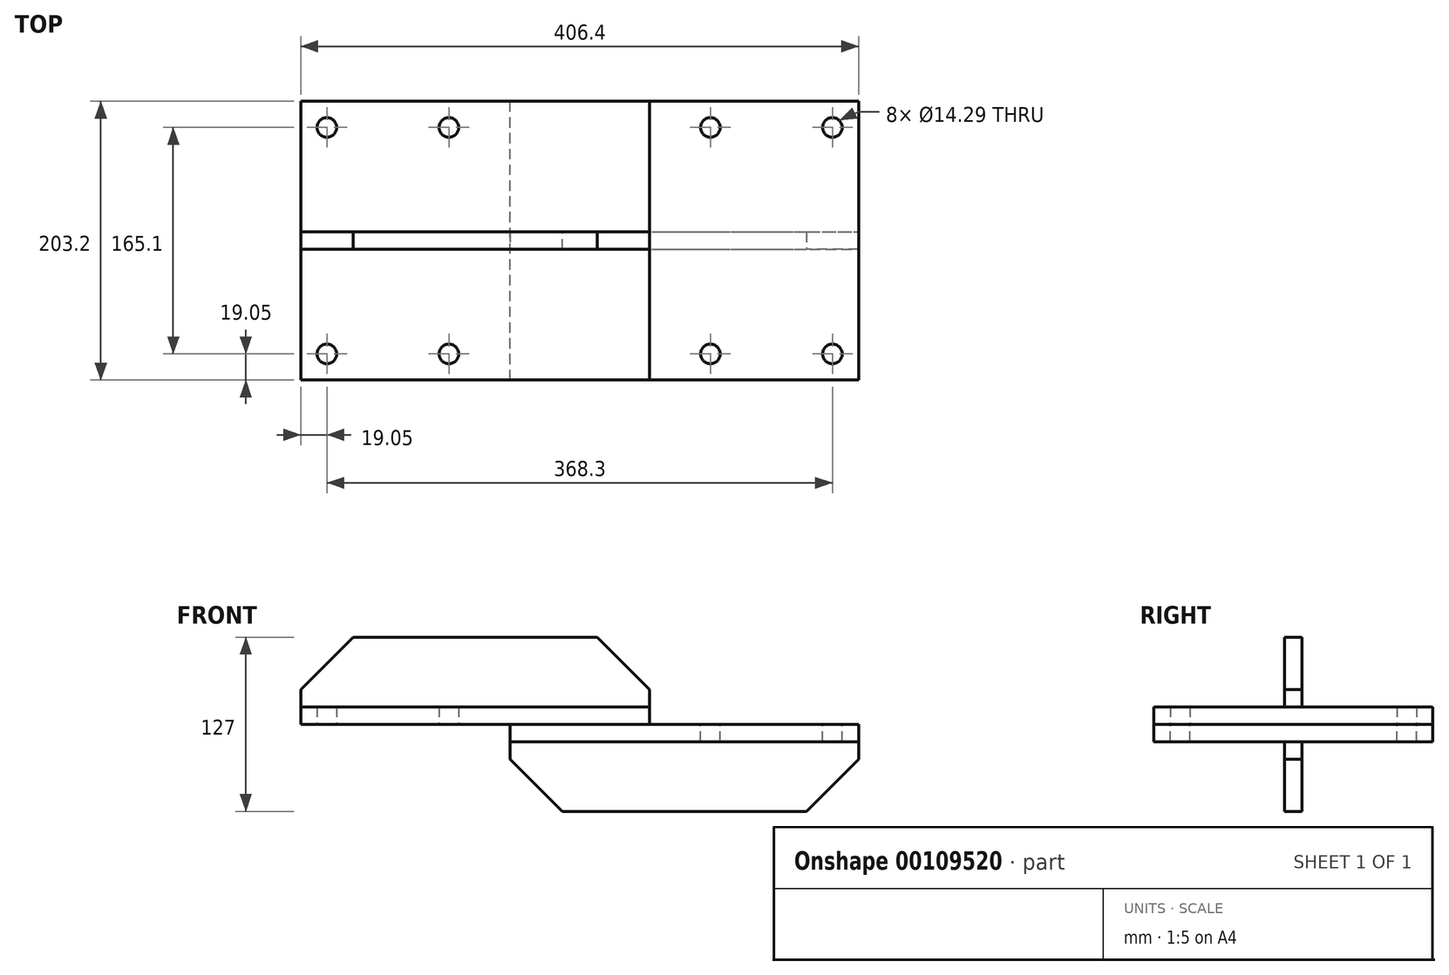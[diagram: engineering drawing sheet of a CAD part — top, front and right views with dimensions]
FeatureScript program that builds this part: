
annotation { "Feature Type Name" : "Feature", "Feature Type Description" : "" }
export const myFeature = defineFeature(function(context is Context, id is Id, definition is map)
    precondition{}
    {
        {
            var Q0;
            Q0=qCreatedBy(makeId("Top.planeOp"),FACE);
            var sketch = newSketch(context, id + "F0", { "sketchPlane" : qUnion([Q0])});
            skLineSegment(sketch, "E0", {"start": v(0, 106.75) * mm, "end": v(0, -105.6) * mm, "construction": true});
            skLineSegment(sketch, "E1.0", {"start": v(-203.2, 106.75) * mm, "end": v(-203.2, -105.6) * mm, "construction": true});
            skLineSegment(sketch, "E2.MirrorCS", {"start": v(203.2, 106.75) * mm, "end": v(203.2, -105.6) * mm, "construction": true});
            skLineSegment(sketch, "E3", {"start": v(-283.64, 0) * mm, "end": v(308.6, 0) * mm, "construction": true});
            skLineSegment(sketch, "E4.0", {"start": v(-283.64, -101.6) * mm, "end": v(308.6, -101.6) * mm, "construction": true});
            skLineSegment(sketch, "E5.bottom", {"start": v(-203.2, -101.6) * mm, "end": v(50.8, -101.6) * mm});
            skLineSegment(sketch, "E5.top", {"start": v(-203.2, 101.6) * mm, "end": v(50.8, 101.6) * mm});
            skLineSegment(sketch, "E5.left", {"start": v(-203.2, -101.6) * mm, "end": v(-203.2, 101.6) * mm});
            skLineSegment(sketch, "E5.right", {"start": v(50.8, -101.6) * mm, "end": v(50.8, 101.6) * mm});
            skLineSegment(sketch, "E6.0", {"start": v(-139.7, -101.6) * mm, "end": v(-139.7, 101.6) * mm, "construction": true});
            skLineSegment(sketch, "E7.0", {"start": v(-184.15, -101.6) * mm, "end": v(-184.15, 101.6) * mm, "construction": true});
            skLineSegment(sketch, "E8.0", {"start": v(-283.64, -82.55) * mm, "end": v(308.6, -82.55) * mm, "construction": true});
            skCircle(sketch, "E9", {"center": v(-184.15, -82.55) * mm, "radius": 7.14 * mm});
            skCircle(sketch, "E10.MirrorC", {"center": v(-95.25, -82.55) * mm, "radius": 7.14 * mm});
            skCircle(sketch, "E11.MirrorC", {"center": v(-95.25, 82.55) * mm, "radius": 7.14 * mm});
            skCircle(sketch, "E12.MirrorC", {"center": v(-184.15, 82.55) * mm, "radius": 7.14 * mm});
            skSolve(sketch);
        }
        {
            var Q0;
            Q0=makeQuery(id+"F0.imprint","IMPRINT",FACE,{"disambiguationData":[TD([[makeQuery(id+"F0.imprint","IMPRINT",EDGE,{"derivedFrom":sQuery(id+"F0.wireOp",EDGE,"E5.bottom")}),1.0]])]});
            extrude(context, id + "F1", {"entities" : qUnion([Q0]), "depth" : 12.7 * mm});
        }
        {
            var Q0;
            Q0=makeQuery(id+"F1.opExtrude","CAP_FACE",FACE,{"disambiguationData":[OSD([sQuery(id+"F0.wireOp",EDGE,"E5.bottom"),sQuery(id+"F0.wireOp",EDGE,"E5.top"),sQuery(id+"F0.wireOp",EDGE,"E5.left"),sQuery(id+"F0.wireOp",EDGE,"E5.right"),sQuery(id+"F0.wireOp",EDGE,"E9"),sQuery(id+"F0.wireOp",EDGE,"E10.MirrorC"),sQuery(id+"F0.wireOp",EDGE,"E11.MirrorC"),sQuery(id+"F0.wireOp",EDGE,"E12.MirrorC")])],"isStart":true});
            var sketch = newSketch(context, id + "F2", { "sketchPlane" : qUnion([Q0])});
            skLineSegment(sketch, "E13.0", {"start": v(-283.64, 101.6) * mm, "end": v(308.6, 101.6) * mm, "construction": true});
            skLineSegment(sketch, "E14.0", {"start": v(203.2, -106.75) * mm, "end": v(203.2, 105.6) * mm, "construction": true});
            skLineSegment(sketch, "E15.bottom", {"start": v(203.2, 101.6) * mm, "end": v(-50.8, 101.6) * mm});
            skLineSegment(sketch, "E15.top", {"start": v(203.2, -101.6) * mm, "end": v(-50.8, -101.6) * mm});
            skLineSegment(sketch, "E15.left", {"start": v(203.2, 101.6) * mm, "end": v(203.2, -101.6) * mm});
            skLineSegment(sketch, "E15.right", {"start": v(-50.8, 101.6) * mm, "end": v(-50.8, -101.6) * mm});
            skLineSegment(sketch, "E16.0", {"start": v(139.7, 101.6) * mm, "end": v(139.7, -101.6) * mm, "construction": true});
            skLineSegment(sketch, "E17.0", {"start": v(184.15, 101.6) * mm, "end": v(184.15, -101.6) * mm, "construction": true});
            skLineSegment(sketch, "E18.0", {"start": v(-283.64, 82.55) * mm, "end": v(308.6, 82.55) * mm, "construction": true});
            skCircle(sketch, "E19", {"center": v(184.15, 82.55) * mm, "radius": 7.14 * mm});
            skCircle(sketch, "E20.MirrorC", {"center": v(95.25, 82.55) * mm, "radius": 7.14 * mm});
            skCircle(sketch, "E21.MirrorC", {"center": v(95.25, -82.55) * mm, "radius": 7.14 * mm});
            skCircle(sketch, "E22.MirrorC", {"center": v(184.15, -82.55) * mm, "radius": 7.14 * mm});
            skSolve(sketch);
        }
        {
            var Q0;
            Q0=qSketchRegion(id+"F2",true);
            extrude(context, id + "F3", {"entities" : qUnion([Q0]), "depth" : 12.7 * mm});
        }
        {
            var Q0;
            Q0=makeQuery(id+"F1.opExtrude","CAP_FACE",FACE,{"disambiguationData":[OSD([sQuery(id+"F0.wireOp",EDGE,"E5.bottom"),sQuery(id+"F0.wireOp",EDGE,"E5.top"),sQuery(id+"F0.wireOp",EDGE,"E5.left"),sQuery(id+"F0.wireOp",EDGE,"E5.right"),sQuery(id+"F0.wireOp",EDGE,"E9"),sQuery(id+"F0.wireOp",EDGE,"E10.MirrorC"),sQuery(id+"F0.wireOp",EDGE,"E11.MirrorC"),sQuery(id+"F0.wireOp",EDGE,"E12.MirrorC")])],"isStart":false});
            var sketch = newSketch(context, id + "F4", { "sketchPlane" : qUnion([Q0])});
            skLineSegment(sketch, "E23.0", {"start": v(-283.64, 0) * mm, "end": v(308.6, 0) * mm, "construction": true});
            skLineSegment(sketch, "E24.0", {"start": v(-203.2, -6.35) * mm, "end": v(50.8, -6.35) * mm});
            skLineSegment(sketch, "E25.0", {"start": v(-203.2, -6.35) * mm, "end": v(-203.2, 6.35) * mm});
            skLineSegment(sketch, "E26.0", {"start": v(50.8, -6.35) * mm, "end": v(50.8, 6.35) * mm});
            skLineSegment(sketch, "E27.MirrorCS", {"start": v(-203.2, 6.35) * mm, "end": v(50.8, 6.35) * mm});
            skPoint(sketch, "E28.orphan", {"position": v(-283.64, 6.35) * mm});
            skPoint(sketch, "E29.orphan", {"position": v(-283.64, -6.35) * mm});
            skPoint(sketch, "E30.orphan", {"position": v(308.6, 6.35) * mm});
            skPoint(sketch, "E31.orphan", {"position": v(308.6, -6.35) * mm});
            skPoint(sketch, "E32.orphan", {"position": v(50.8, 101.6) * mm});
            skPoint(sketch, "E33.orphan", {"position": v(50.8, -101.6) * mm});
            skPoint(sketch, "E34.orphan", {"position": v(-203.2, -101.6) * mm});
            skPoint(sketch, "E35.orphan", {"position": v(-203.2, 101.6) * mm});
            skSolve(sketch);
        }
        {
            var Q0;
            Q0=qSketchRegion(id+"F4",true);
            extrude(context, id + "F5", {"entities" : qUnion([Q0]), "depth" : 50.8 * mm});
        }
        {
            var Q0;
            Q0=makeQuery(id+"F5.opExtrude","CAP_EDGE",EDGE,{"disambiguationData":[OSD([sQuery(id+"F4.wireOp",EDGE,"E25.0")])],"isStart":false});
            var Q1;
            Q1=makeQuery(id+"F5.opExtrude","CAP_EDGE",EDGE,{"disambiguationData":[OSD([sQuery(id+"F4.wireOp",EDGE,"E26.0")])],"isStart":false});
            chamfer(context, id + "F6", {"entities" : qUnion([Q0, Q1]), "width" : 38.1 * mm, "tangentPropagation" : true});
        }
        {
            var Q0;
            Q0=makeQuery(id+"F3.opExtrude","CAP_FACE",FACE,{"disambiguationData":[OSD([sQuery(id+"F2.wireOp",EDGE,"E15.bottom"),sQuery(id+"F2.wireOp",EDGE,"E15.top"),sQuery(id+"F2.wireOp",EDGE,"E15.left"),sQuery(id+"F2.wireOp",EDGE,"E15.right"),sQuery(id+"F2.wireOp",EDGE,"E19"),sQuery(id+"F2.wireOp",EDGE,"E20.MirrorC"),sQuery(id+"F2.wireOp",EDGE,"E21.MirrorC"),sQuery(id+"F2.wireOp",EDGE,"E22.MirrorC")])],"isStart":false});
            var sketch = newSketch(context, id + "F7", { "sketchPlane" : qUnion([Q0])});
            skLineSegment(sketch, "E36.0", {"start": v(-283.64, 0) * mm, "end": v(308.6, 0) * mm, "construction": true});
            skLineSegment(sketch, "E37.0", {"start": v(-50.8, 101.6) * mm, "end": v(-50.8, -101.6) * mm});
            skLineSegment(sketch, "E38.0", {"start": v(203.2, -106.75) * mm, "end": v(203.2, 105.6) * mm});
            skLineSegment(sketch, "E39.0", {"start": v(-283.64, -6.35) * mm, "end": v(308.6, -6.35) * mm});
            skLineSegment(sketch, "E40.MirrorCS", {"start": v(-283.64, 6.35) * mm, "end": v(308.6, 6.35) * mm});
            skSolve(sketch);
        }
        {
            var Q0;
            {var subQ0=sQuery(id+"F7.wireOp",EDGE,"E40.MirrorCS");var subQ3=sQuery(id+"F7.wireOp",EDGE,"E37.0");var subQ4=makeQuery(id+"F7.imprint","INTERSECT",VERTEX,{"derivedFrom":[subQ3,subQ0]});Q0=makeQuery(id+"F7.imprint","IMPRINT",FACE,{"disambiguationData":[TD([[makeQuery(id+"F7.imprint","IMPRINT",EDGE,{"disambiguationData":[TD([[subQ4,-1.0]])],"derivedFrom":subQ3}),1.0]])]});}
            extrude(context, id + "F8", {"entities" : qUnion([Q0]), "depth" : 50.8 * mm});
        }
        {
            var Q0;
            Q0=makeQuery(id+"F8.opExtrude","CAP_EDGE",EDGE,{"disambiguationData":[OSD([sQuery(id+"F7.wireOp",EDGE,"E38.0")])],"isStart":false});
            var Q1;
            Q1=makeQuery(id+"F8.opExtrude","CAP_EDGE",EDGE,{"disambiguationData":[OSD([sQuery(id+"F7.wireOp",EDGE,"E37.0")])],"isStart":false});
            chamfer(context, id + "F9", {"entities" : qUnion([Q0, Q1]), "width" : 38.1 * mm, "tangentPropagation" : true});
        }
    });
